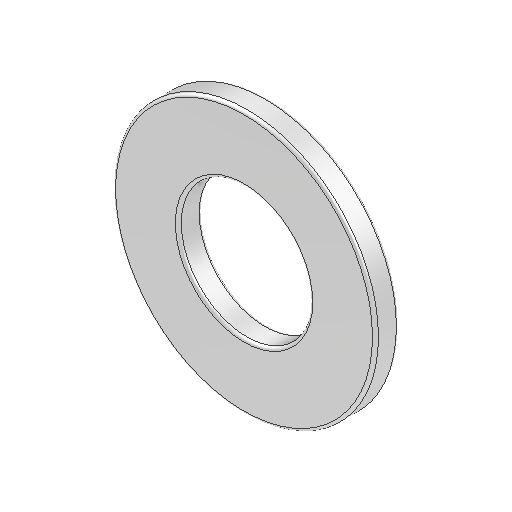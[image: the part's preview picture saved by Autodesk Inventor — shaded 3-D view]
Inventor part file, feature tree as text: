
AUTODESK INVENTOR PART (.ipt)
format: ipt  version: 2025 (Build 290162000, 162)  size: 133,632 bytes
history: native  units: mm
features: fillet x2, other x1, extrude x1, sketch x1
ambient origin geometry x8: Origin, YZ Plane, XZ Plane, XY Plane, X Axis, Y Axis, Z Axis, Center Point
bodies: Body1 (feature_tree)
feature tree (5):
  other  "Sólido1"
  extrude  "Extrusão1"  Depth=0.1mm
  fillet  "Arredondamento1"  Radius=0.8mm
  fillet  "Arredondamento2"  Radius=0.1mm
  sketch  "Esboço1"  dims[d0=4.4mm d1=8.8mm d2=0.8mm d3=0.0mm d4=0.1mm d5=0.1mm]
